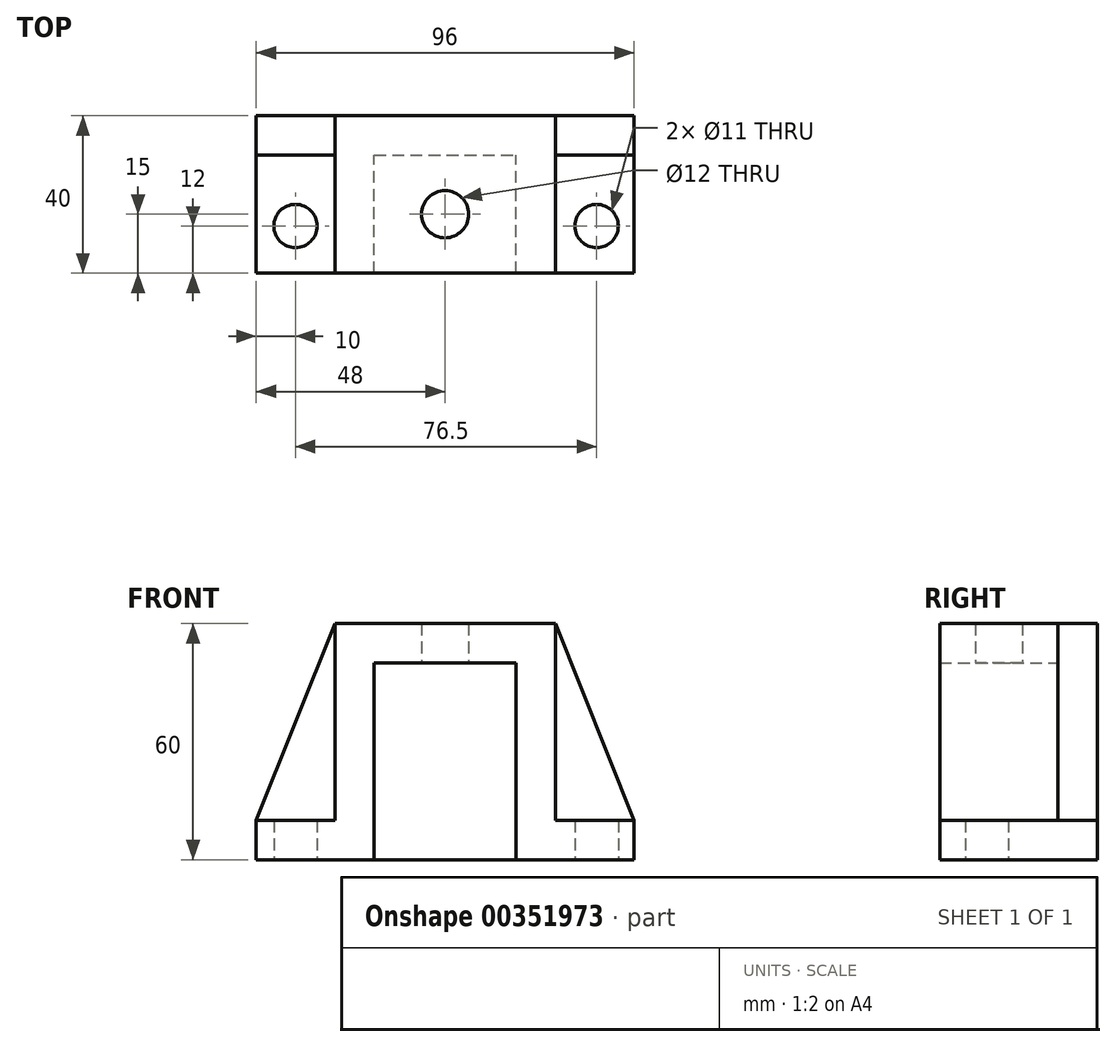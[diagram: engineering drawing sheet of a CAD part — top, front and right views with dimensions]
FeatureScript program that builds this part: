
annotation { "Feature Type Name" : "Feature", "Feature Type Description" : "" }
export const myFeature = defineFeature(function(context is Context, id is Id, definition is map)
    precondition{}
    {
        {
            var Q0;
            Q0=qCreatedBy(makeId("Front.planeOp"),FACE);
            var sketch = newSketch(context, id + "F0", { "sketchPlane" : qUnion([Q0])});
            skLineSegment(sketch, "E0", {"start": v(-48, 0) * mm, "end": v(48, 0) * mm});
            skLineSegment(sketch, "E1", {"start": v(0, 0) * mm, "end": v(48, 0) * mm});
            skLineSegment(sketch, "E2", {"start": v(-48, 0) * mm, "end": v(-48, 10) * mm});
            skLineSegment(sketch, "E3", {"start": v(48, 0) * mm, "end": v(48, 10) * mm});
            skLineSegment(sketch, "E4", {"start": v(-48, 10) * mm, "end": v(-28, 10) * mm});
            skLineSegment(sketch, "E5", {"start": v(-28, 10) * mm, "end": v(-28, 60) * mm});
            skLineSegment(sketch, "E6", {"start": v(-28, 60) * mm, "end": v(28, 60) * mm});
            skPoint(sketch, "E7", {"position": v(0, 60) * mm});
            skPoint(sketch, "E7.positionSnap0", {"position": v(18, 60) * mm});
            skLineSegment(sketch, "E8", {"start": v(48, 10) * mm, "end": v(28, 10) * mm});
            skLineSegment(sketch, "E9", {"start": v(28, 10) * mm, "end": v(28, 60) * mm});
            skPoint(sketch, "E10.orphan", {"position": v(64, 60) * mm});
            skLineSegment(sketch, "E11", {"start": v(28, 60) * mm, "end": v(48, 10) * mm});
            skLineSegment(sketch, "E12", {"start": v(-28, 60) * mm, "end": v(-48, 10) * mm});
            skPoint(sketch, "E13", {"position": v(-18, 60) * mm});
            skLineSegment(sketch, "E14", {"start": v(-18, 50) * mm, "end": v(-18, 0) * mm});
            skLineSegment(sketch, "E15", {"start": v(18, 50) * mm, "end": v(18, 0) * mm});
            skPoint(sketch, "E15.endSnap0", {"position": v(24, 0) * mm});
            skPoint(sketch, "E16", {"position": v(18, 50) * mm});
            skLineSegment(sketch, "E17", {"start": v(18, 50) * mm, "end": v(-18, 50) * mm});
            skSolve(sketch);
        }
        {
            var Q0;
            Q0=qCreatedBy(makeId("Top.planeOp"),FACE);
            var sketch = newSketch(context, id + "F1", { "sketchPlane" : qUnion([Q0])});
            skLineSegment(sketch, "E18", {"start": v(48, -40) * mm, "end": v(-48, -40) * mm});
            skPoint(sketch, "E19", {"position": v(-38, -40) * mm});
            skPoint(sketch, "E20", {"position": v(38, -40) * mm});
            skLineSegment(sketch, "E21", {"start": v(48, -40) * mm, "end": v(48, -20) * mm});
            skLineSegment(sketch, "E22", {"start": v(48, 0) * mm, "end": v(-48, 0) * mm});
            skLineSegment(sketch, "E23", {"start": v(-48, -40) * mm, "end": v(-48, 0) * mm});
            skLineSegment(sketch, "E24", {"start": v(48, -10) * mm, "end": v(28, -10) * mm});
            skPoint(sketch, "E25", {"position": v(28, -40) * mm});
            skPoint(sketch, "E26", {"position": v(-28, -40) * mm});
            skLineSegment(sketch, "E27", {"start": v(28, -40) * mm, "end": v(28, 0) * mm});
            skLineSegment(sketch, "E28", {"start": v(-28, -40) * mm, "end": v(-28, 0) * mm});
            skLineSegment(sketch, "E29.trimOffspring", {"start": v(48, -10) * mm, "end": v(48, 0) * mm});
            skPoint(sketch, "E30", {"position": v(48, -28) * mm});
            skLineSegment(sketch, "E31", {"start": v(48, 0) * mm, "end": v(48, -40) * mm});
            skPoint(sketch, "E32", {"position": v(38.5, -28) * mm});
            skPoint(sketch, "E33", {"position": v(-38, -28) * mm});
            skCircle(sketch, "E34", {"center": v(38.5, -28) * mm, "radius": 5.5 * mm});
            skCircle(sketch, "E35", {"center": v(-38, -28) * mm, "radius": 5.5 * mm});
            skPoint(sketch, "E36", {"position": v(33, -28) * mm});
            skPoint(sketch, "E37", {"position": v(-32.5, -28) * mm});
            skLineSegment(sketch, "E38.trimOffspring", {"start": v(-28, -10) * mm, "end": v(-48, -10) * mm});
            skLineSegment(sketch, "E39", {"start": v(18, -10) * mm, "end": v(-18, -10) * mm, "construction": true});
            skLineSegment(sketch, "E40", {"start": v(0, -0.34) * mm, "end": v(0, 57.35) * mm, "construction": true});
            skPoint(sketch, "E41", {"position": v(0, -25) * mm});
            skPoint(sketch, "E42", {"position": v(0, 0) * mm});
            skCircle(sketch, "E43", {"center": v(0, -25) * mm, "radius": 6 * mm});
            skPoint(sketch, "E44", {"position": v(-6, -25.11) * mm});
            skPoint(sketch, "E45", {"position": v(18, -40) * mm});
            skPoint(sketch, "E46", {"position": v(-18, -40) * mm});
            skLineSegment(sketch, "E47", {"start": v(18, -40) * mm, "end": v(18, -10) * mm, "construction": true});
            skLineSegment(sketch, "E48", {"start": v(-18, -40) * mm, "end": v(-18, -10) * mm, "construction": true});
            skLineSegment(sketch, "E49.trimOffspring", {"start": v(-38, 39.66) * mm, "end": v(-38, 56.86) * mm, "construction": true});
            skLineSegment(sketch, "E50.trimOffspring", {"start": v(-43.5, -28) * mm, "end": v(-48, -28) * mm, "construction": true});
            skLineSegment(sketch, "E51.trimOffspring", {"start": v(38, 39.66) * mm, "end": v(38, 58.83) * mm, "construction": true});
            skPoint(sketch, "E52.orphan", {"position": v(-18, 0) * mm});
            skSolve(sketch);
        }
        {
            var Q0;
            {var subQ1=sQuery(id+"F0.wireOp",EDGE,"E2");Q0=makeQuery(id+"F0.imprint","IMPRINT",FACE,{"disambiguationData":[TD([[makeQuery(id+"F0.imprint","IMPRINT",EDGE,{"derivedFrom":subQ1}),-1.0]])]});}
            extrude(context, id + "F2", {"entities" : qUnion([Q0]), "depth" : 40 * mm});
        }
        {
            var Q0;
            Q0=makeQuery(id+"F0.imprint","IMPRINT",FACE,{"disambiguationData":[TD([[makeQuery(id+"F0.imprint","IMPRINT",EDGE,{"derivedFrom":sQuery(id+"F0.wireOp",EDGE,"E8")}),-1.0]])]});
            var Q1;
            Q1=makeQuery(id+"F0.imprint","IMPRINT",FACE,{"disambiguationData":[TD([[makeQuery(id+"F0.imprint","IMPRINT",EDGE,{"derivedFrom":sQuery(id+"F0.wireOp",EDGE,"E4")}),1.0]])]});
            var Q2;
            {var subQ1=sQuery(id+"F0.wireOp",EDGE,"E14");Q2=makeQuery(id+"F0.imprint","IMPRINT",FACE,{"disambiguationData":[TD([[makeQuery(id+"F0.imprint","IMPRINT",EDGE,{"derivedFrom":subQ1}),1.0]])]});}
            extrude(context, id + "F3", {"entities" : qUnion([Q0, Q1, Q2]), "operationType" : NewBodyOperationType.ADD, "depth" : 10 * mm});
        }
        {
            var Q0;
            Q0=sQuery(id+"F1.wireOp",VERTEX,"E41");
            var Q1;
            Q1=makeQuery(id+"F2.opExtrude","SWEPT_BODY",BODY,{"disambiguationData":[OSD([sQuery(id+"F0.wireOp",EDGE,"E0"),sQuery(id+"F0.wireOp",EDGE,"E1"),sQuery(id+"F0.wireOp",EDGE,"E2"),sQuery(id+"F0.wireOp",EDGE,"E3"),sQuery(id+"F0.wireOp",EDGE,"E4"),sQuery(id+"F0.wireOp",EDGE,"E5"),sQuery(id+"F0.wireOp",EDGE,"E6"),sQuery(id+"F0.wireOp",EDGE,"E8"),sQuery(id+"F0.wireOp",EDGE,"E9"),sQuery(id+"F0.wireOp",EDGE,"E14"),sQuery(id+"F0.wireOp",EDGE,"E15"),sQuery(id+"F0.wireOp",EDGE,"E17")])]});
            hole(context, id + "F4", {"style" : HoleStyle.SIMPLE, "endStyle" : HoleEndStyle.THROUGH, "oppositeDirection" : true, "holeDiameter" : 12 * mm, "isTappedThrough" : true, "tappedDepth" : 12 * mm, "tapClearance" : 3, "locations" : qUnion([Q0]), "scope" : qUnion([Q1])});
        }
        {
            var Q0;
            Q0=sQuery(id+"F1.wireOp",VERTEX,"E32");
            var Q1;
            Q1=makeQuery(id+"F2.opExtrude","SWEPT_BODY",BODY,{"disambiguationData":[OSD([sQuery(id+"F0.wireOp",EDGE,"E0"),sQuery(id+"F0.wireOp",EDGE,"E1"),sQuery(id+"F0.wireOp",EDGE,"E2"),sQuery(id+"F0.wireOp",EDGE,"E3"),sQuery(id+"F0.wireOp",EDGE,"E4"),sQuery(id+"F0.wireOp",EDGE,"E5"),sQuery(id+"F0.wireOp",EDGE,"E6"),sQuery(id+"F0.wireOp",EDGE,"E8"),sQuery(id+"F0.wireOp",EDGE,"E9"),sQuery(id+"F0.wireOp",EDGE,"E14"),sQuery(id+"F0.wireOp",EDGE,"E15"),sQuery(id+"F0.wireOp",EDGE,"E17")])]});
            hole(context, id + "F5", {"style" : HoleStyle.SIMPLE, "endStyle" : HoleEndStyle.THROUGH, "oppositeDirection" : true, "holeDiameter" : 11 * mm, "isTappedThrough" : true, "tappedDepth" : 12 * mm, "tapClearance" : 3, "locations" : qUnion([Q0]), "scope" : qUnion([Q1])});
        }
        {
            var Q0;
            Q0=sQuery(id+"F1.wireOp",VERTEX,"E33");
            var Q1;
            Q1=makeQuery(id+"F2.opExtrude","SWEPT_BODY",BODY,{"disambiguationData":[OSD([sQuery(id+"F0.wireOp",EDGE,"E0"),sQuery(id+"F0.wireOp",EDGE,"E1"),sQuery(id+"F0.wireOp",EDGE,"E2"),sQuery(id+"F0.wireOp",EDGE,"E3"),sQuery(id+"F0.wireOp",EDGE,"E4"),sQuery(id+"F0.wireOp",EDGE,"E5"),sQuery(id+"F0.wireOp",EDGE,"E6"),sQuery(id+"F0.wireOp",EDGE,"E8"),sQuery(id+"F0.wireOp",EDGE,"E9"),sQuery(id+"F0.wireOp",EDGE,"E14"),sQuery(id+"F0.wireOp",EDGE,"E15"),sQuery(id+"F0.wireOp",EDGE,"E17")])]});
            hole(context, id + "F6", {"style" : HoleStyle.SIMPLE, "endStyle" : HoleEndStyle.THROUGH, "oppositeDirection" : true, "holeDiameter" : 11 * mm, "isTappedThrough" : true, "tappedDepth" : 12 * mm, "tapClearance" : 3, "locations" : qUnion([Q0]), "scope" : qUnion([Q1])});
        }
    });
